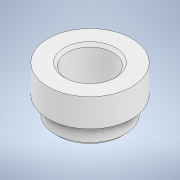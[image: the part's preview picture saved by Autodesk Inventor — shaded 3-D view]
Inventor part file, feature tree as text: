
AUTODESK INVENTOR PART (.ipt)
format: ipt  version: 2020 (Build 240168000, 168)  size: 134,144 bytes
history: native  units: mm
features: extrude x3, other x1, sketch x1, chamfer x1
ambient origin geometry x8: Origin, YZ Plane, XZ Plane, XY Plane, X Axis, Y Axis, Z Axis, Center Point
bodies: Body1 (feature_tree)
feature tree (6):
  other  "Bryła1"
  sketch  "Szkic1"
  extrude  "Wyciągnięcie proste1"  Depth=30.0mm
  extrude  "Wyciągnięcie proste2"  Depth=16.5mm
  extrude  "Wyciągnięcie proste3"  Depth=25.0mm
  chamfer  "Faza1"  Distance=17.0mm
